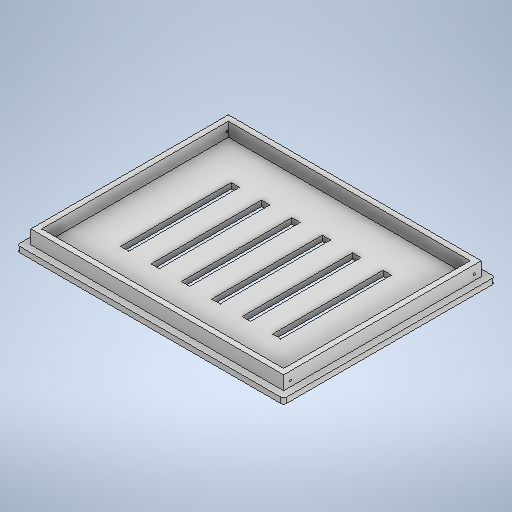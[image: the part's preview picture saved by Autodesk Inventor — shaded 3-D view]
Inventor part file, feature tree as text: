
AUTODESK INVENTOR PART (.ipt)
format: ipt  version: 2025 (Build 290162010, 162A)  size: 345,088 bytes
history: native  units: in
note: dims shown in document units (in); Inventor stores cm internally (conversion verified against a paired STEP export)
features: extrude x4, sketch x4, fillet x1
ambient origin geometry x8: Origin, YZ Plane, XZ Plane, XY Plane, X Axis, Y Axis, Z Axis, Center Point
bodies: Volumenkörper1 (feature_tree)
feature tree (9):
  extrude  "Extrusion1"  Depth=3.563in
  extrude  "Extrusion7"  Depth=0.1181in
  extrude  "Extrusion8"  Depth=0.1181in
  fillet  "Rundung2"  Radius=0.0787in
  extrude  "Extrusion9"  Depth=0.0984in
  sketch  "Skizze1"  dims[d0=2.7756in d1=3.563in]
  sketch  "Skizze7"  dims[d2=0.1181in d3=0.1181in]
  sketch  "Skizze8"  dims[d4=0.1181in d5=0.1181in d6=0.0787in d7=0.0in]
  sketch  "Skizze9"  dims[d51=0.0984in d52=0.0984in d53=0.0984in d54=0.0984in d55=0.0787in d56=0.0787in d57=0.0787in d58=0.0787in d59=0.1969in d60=0.0in d61=0.0787in d62=0.1969in d63=0.0787in d64=0.1969in d65=0.0315in d66=0.0in d67=0.0in d68=0.0394in d69=0.1181in d70=0.315in d71=0.315in d72=0.315in d73=1.5748in d74=0.5413in d75=0.5807in d76=0.3937in d77=0.0in d78=0.315in d79=0.315in]
